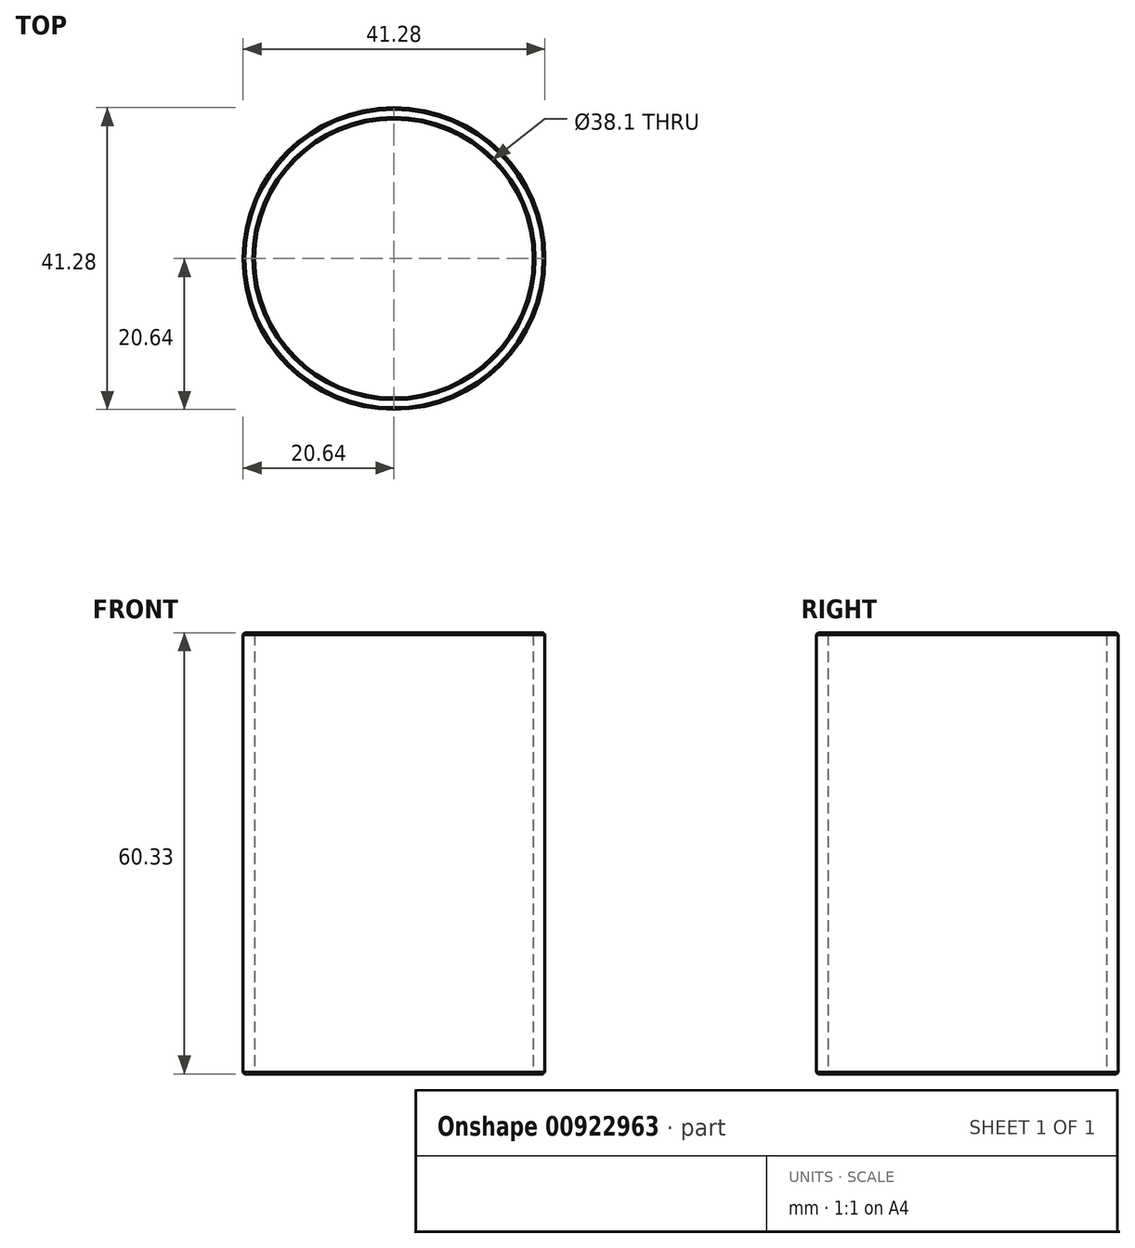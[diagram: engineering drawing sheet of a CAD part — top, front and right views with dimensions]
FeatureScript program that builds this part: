
annotation { "Feature Type Name" : "Feature", "Feature Type Description" : "" }
export const myFeature = defineFeature(function(context is Context, id is Id, definition is map)
    precondition{}
    {
        {
            var Q0;
            Q0=qCreatedBy(makeId("Front.planeOp"),FACE);
            var sketch = newSketch(context, id + "F0", { "sketchPlane" : qUnion([Q0])});
            skLineSegment(sketch, "E0", {"start": v(0, 0) * mm, "end": v(0, 60.54) * mm, "construction": true});
            skLineSegment(sketch, "E1.bottom", {"start": v(-20.64, 60.33) * mm, "end": v(-19.05, 60.33) * mm});
            skLineSegment(sketch, "E1.top", {"start": v(-20.64, 0) * mm, "end": v(-19.05, 0) * mm});
            skLineSegment(sketch, "E1.left", {"start": v(-20.64, 60.33) * mm, "end": v(-20.64, 0) * mm});
            skLineSegment(sketch, "E1.right", {"start": v(-19.05, 60.33) * mm, "end": v(-19.05, 0) * mm});
            skSolve(sketch);
        }
        {
            var Q0;
            Q0 = qSketchRegion(id + "F0", true);
            var Q1;
            Q1=sQuery(id+"F0.wireOp",EDGE,"E0");
            revolve(context, id + "F1", {"surfaceOperationType" : NewSurfaceOperationType.NEW, "entities" : qUnion([Q0]), "axis" : qUnion([Q1]), "revolveType" : RevolveType.FULL});
        }
        {
            var Q0;
            Q0=makeQuery(id+"F1.opRevolve","SWEPT_EDGE",EDGE,{"disambiguationData":[OSD([sQuery(id+"F0.wireOp",EDGE,"E1.bottom"),sQuery(id+"F0.wireOp",EDGE,"E1.right")])]});
            var Q1;
            Q1=makeQuery(id+"F1.opRevolve","SWEPT_EDGE",EDGE,{"disambiguationData":[OSD([sQuery(id+"F0.wireOp",EDGE,"E1.bottom"),sQuery(id+"F0.wireOp",EDGE,"E1.left")])]});
            var Q2;
            Q2=makeQuery(id+"F1.opRevolve","SWEPT_EDGE",EDGE,{"disambiguationData":[OSD([sQuery(id+"F0.wireOp",EDGE,"E1.top"),sQuery(id+"F0.wireOp",EDGE,"E1.right")])]});
            var Q3;
            Q3=makeQuery(id+"F1.opRevolve","SWEPT_EDGE",EDGE,{"disambiguationData":[OSD([sQuery(id+"F0.wireOp",EDGE,"E1.top"),sQuery(id+"F0.wireOp",EDGE,"E1.left")])]});
            chamfer(context, id + "F2", {"entities" : qUnion([Q0, Q1, Q2, Q3]), "width" : 0.25 * mm, "tangentPropagation" : true});
        }
    });
